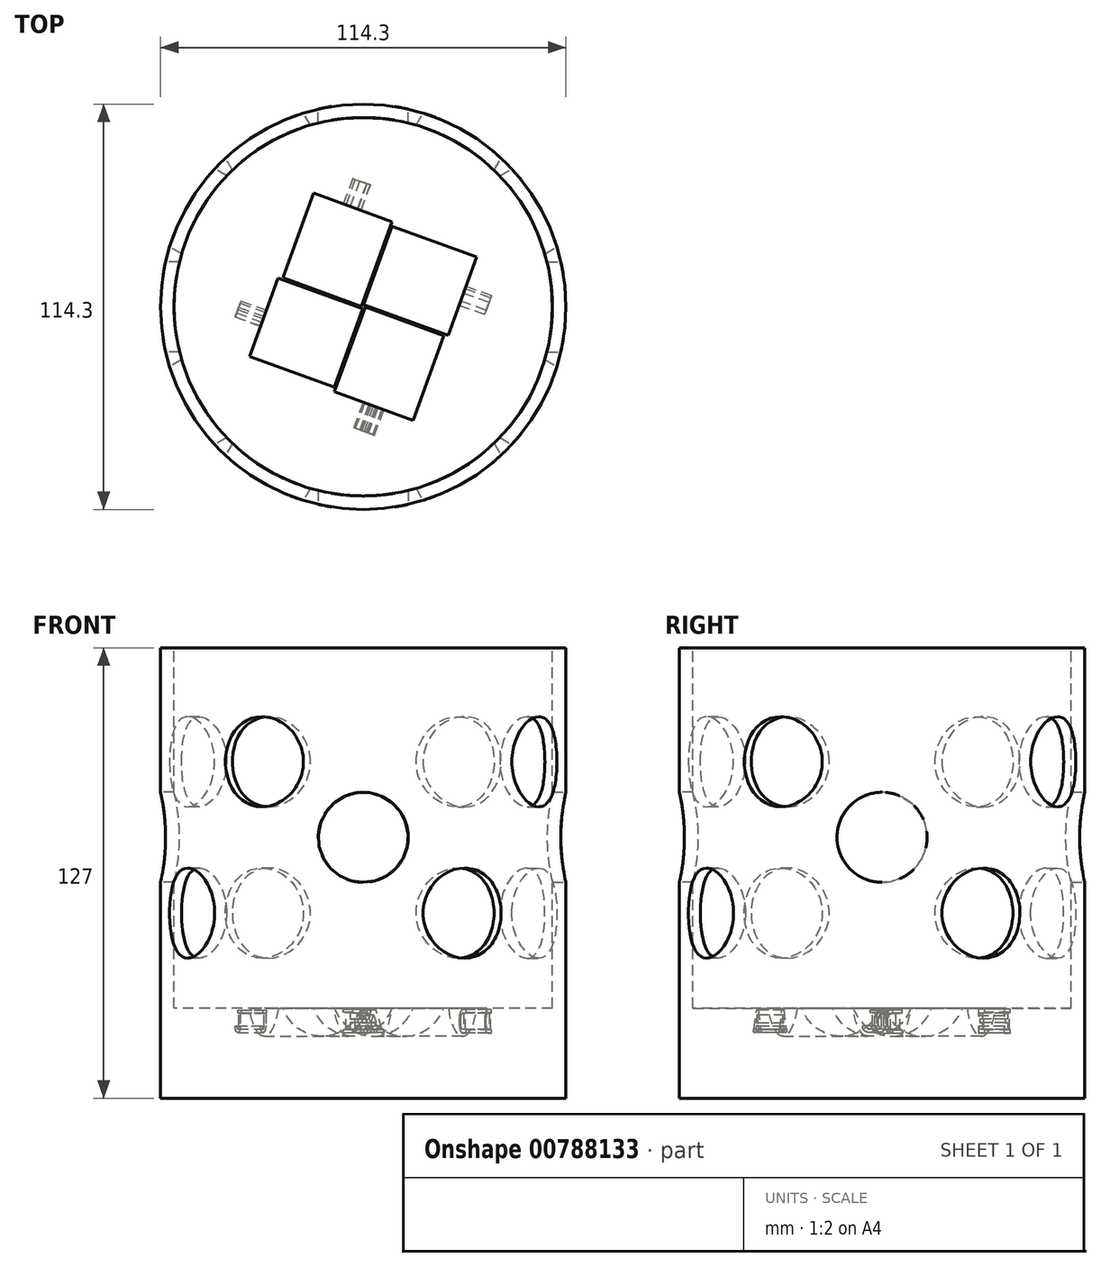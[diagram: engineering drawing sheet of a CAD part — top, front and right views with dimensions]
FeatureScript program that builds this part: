
annotation { "Feature Type Name" : "Feature", "Feature Type Description" : "" }
export const myFeature = defineFeature(function(context is Context, id is Id, definition is map)
    precondition{}
    {
        {
            var Q0;
            Q0=qCreatedBy(makeId("Top.planeOp"),FACE);
            var sketch = newSketch(context, id + "F0", { "sketchPlane" : qUnion([Q0])});
            skCircle(sketch, "E0", {"center": v(0, 0) * mm, "radius": 57.15 * mm});
            skSolve(sketch);
        }
        {
            var Q0;
            Q0=makeQuery(id+"F0.imprint","IMPRINT",FACE,{"disambiguationData":[TD([[makeQuery(id+"F0.imprint","IMPRINT",EDGE,{"derivedFrom":sQuery(id+"F0.wireOp",EDGE,"E0")}),1.0]])]});
            var Q1;
            Q1=sQuery(id+"F0.wireOp",EDGE,"E0");
            extrude(context, id + "F1", {"entities" : qUnion([Q0]), "surfaceEntities" : qUnion([Q1]), "depth" : 127 * mm, "offsetDistance" : 25.4 * mm});
        }
        {
            var Q0;
            Q0=makeQuery(id+"F1.opExtrude","CAP_FACE",FACE,{"disambiguationData":[OSD([sQuery(id+"F0.wireOp",EDGE,"E0")])],"isStart":false});
            var sketch = newSketch(context, id + "F2", { "sketchPlane" : qUnion([Q0])});
            skCircle(sketch, "E1", {"center": v(0, 0) * mm, "radius": 53.34 * mm});
            skSolve(sketch);
        }
        {
            var Q0;
            Q0=makeQuery(id+"F2.imprint","IMPRINT",FACE,{"disambiguationData":[TD([[makeQuery(id+"F2.imprint","IMPRINT",EDGE,{"derivedFrom":sQuery(id+"F2.wireOp",EDGE,"E1")}),1.0]])]});
            extrude(context, id + "F3", {"entities" : qUnion([Q0]), "operationType" : NewBodyOperationType.REMOVE, "oppositeDirection" : true, "depth" : 101.6 * mm, "offsetDistance" : 25.4 * mm});
        }
        {
            var Q0;
            Q0=qCreatedBy(makeId("Front.planeOp"),FACE);
            cPlane(context, id + "F4", {"entities" : qUnion([Q0]), "cplaneType" : CPlaneType.OFFSET, "offset" : 57.15 * mm, "width" : 152.4 * mm, "height" : 152.4 * mm});
        }
        {
            var Q0;
            Q0=qCreatedBy(id+"F4.planeOp",FACE);
            var sketch = newSketch(context, id + "F5", { "sketchPlane" : qUnion([Q0])});
            skCircle(sketch, "E2", {"center": v(0, 73.56) * mm, "radius": 12.7 * mm});
            skSolve(sketch);
        }
        {
            var Q0;
            Q0=makeQuery(id+"F5.imprint","IMPRINT",FACE,{"disambiguationData":[TD([[makeQuery(id+"F5.imprint","IMPRINT",EDGE,{"derivedFrom":sQuery(id+"F5.wireOp",EDGE,"E2")}),1.0]])]});
            extrude(context, id + "F6", {"entities" : qUnion([Q0]), "oppositeDirection" : true, "depth" : 25.4 * mm, "offsetDistance" : 25.4 * mm});
        }
        {
            var Q0;
            Q0=qCreatedBy(makeId("Front.planeOp"),FACE);
            var sketch = newSketch(context, id + "F7", { "sketchPlane" : qUnion([Q0])});
            skLineSegment(sketch, "E3", {"start": v(0, 0) * mm, "end": v(0, 71.78) * mm});
            skSolve(sketch);
        }
        {
            var Q0;
            Q0=makeQuery(id+"F6.opExtrude","SWEPT_BODY",BODY,{"disambiguationData":[OSD([sQuery(id+"F5.wireOp",EDGE,"E2")])]});
            var Q1;
            Q1=sQuery(id+"F7.wireOp",EDGE,"E3");
            circularPattern(context, id + "F8", {"entities" : qUnion([Q0]), "axis" : qUnion([Q1]), "angle" : 360 * degree, "instanceCount" : 4, "equalSpace" : true});
        }
        {
            var Q0;
            Q0=makeQuery(id+"F6.opExtrude","SWEPT_BODY",BODY,{"disambiguationData":[OSD([sQuery(id+"F5.wireOp",EDGE,"E2")])]});
            var Q1;
            Q1=makeQuery(id+"F8.opPattern","COPY",BODY,{"derivedFrom":makeQuery(id+"F6.opExtrude","SWEPT_BODY",BODY,{"disambiguationData":[OSD([sQuery(id+"F5.wireOp",EDGE,"E2")])]}),"instanceName":"3"});
            var Q2;
            Q2=makeQuery(id+"F8.opPattern","COPY",BODY,{"derivedFrom":makeQuery(id+"F6.opExtrude","SWEPT_BODY",BODY,{"disambiguationData":[OSD([sQuery(id+"F5.wireOp",EDGE,"E2")])]}),"instanceName":"2"});
            var Q3;
            Q3=makeQuery(id+"F8.opPattern","COPY",BODY,{"derivedFrom":makeQuery(id+"F6.opExtrude","SWEPT_BODY",BODY,{"disambiguationData":[OSD([sQuery(id+"F5.wireOp",EDGE,"E2")])]}),"instanceName":"1"});
            var Q4;
            Q4=makeQuery(id+"F1.opExtrude","SWEPT_BODY",BODY,{"disambiguationData":[OSD([sQuery(id+"F0.wireOp",EDGE,"E0")])]});
            booleanBodies(context, id + "F9", {"operationType" : BooleanOperationType.SUBTRACTION, "tools" : qUnion([Q0, Q1, Q2, Q3]), "targets" : qUnion([Q4])});
        }
        {
            var Q0;
            Q0=makeQuery(id+"F1.opExtrude","CAP_EDGE",EDGE,{"disambiguationData":[OSD([sQuery(id+"F0.wireOp",EDGE,"E0")])],"isStart":false});
            cPlane(context, id + "F10", {"entities" : qUnion([Q0]), "cplaneType" : CPlaneType.LINE_ANGLE, "offset" : 25.4 * mm, "angle" : 60 * degree, "width" : 152.4 * mm, "height" : 152.4 * mm});
        }
        {
            var Q0;
            Q0=qCreatedBy(id+"F10.planeOp",FACE);
            cPlane(context, id + "F11", {"entities" : qUnion([Q0]), "cplaneType" : CPlaneType.OFFSET, "offset" : 57.15 * mm, "width" : 152.4 * mm, "height" : 152.4 * mm});
        }
        {
            var Q0;
            Q0=qCreatedBy(id+"F11.planeOp",FACE);
            var sketch = newSketch(context, id + "F12", { "sketchPlane" : qUnion([Q0])});
            skCircle(sketch, "E4", {"center": v(0, 94.86) * mm, "radius": 12.7 * mm});
            skSolve(sketch);
        }
        {
            var Q0;
            Q0=makeQuery(id+"F12.imprint","IMPRINT",FACE,{"disambiguationData":[TD([[makeQuery(id+"F12.imprint","IMPRINT",EDGE,{"derivedFrom":sQuery(id+"F12.wireOp",EDGE,"E4")}),1.0]])]});
            extrude(context, id + "F13", {"entities" : qUnion([Q0]), "oppositeDirection" : true, "depth" : 25.4 * mm, "offsetDistance" : 25.4 * mm});
        }
        {
            var Q0;
            Q0=makeQuery(id+"F13.opExtrude","SWEPT_BODY",BODY,{"disambiguationData":[OSD([sQuery(id+"F12.wireOp",EDGE,"E4")])]});
            var Q1;
            Q1=makeQuery(id+"F1.opExtrude","SWEPT_FACE",FACE,{"disambiguationData":[OSD([sQuery(id+"F0.wireOp",EDGE,"E0")])]});
            circularPattern(context, id + "F14", {"entities" : qUnion([Q0]), "axis" : qUnion([Q1]), "angle" : 360 * degree, "instanceCount" : 4, "equalSpace" : true, "isCentered" : true});
        }
        {
            var Q0;
            Q0=makeQuery(id+"F14.opPattern","COPY",BODY,{"derivedFrom":makeQuery(id+"F13.opExtrude","SWEPT_BODY",BODY,{"disambiguationData":[OSD([sQuery(id+"F12.wireOp",EDGE,"E4")])]}),"instanceName":"-1"});
            var Q1;
            Q1=makeQuery(id+"F13.opExtrude","SWEPT_BODY",BODY,{"disambiguationData":[OSD([sQuery(id+"F12.wireOp",EDGE,"E4")])]});
            var Q2;
            Q2=makeQuery(id+"F14.opPattern","COPY",BODY,{"derivedFrom":makeQuery(id+"F13.opExtrude","SWEPT_BODY",BODY,{"disambiguationData":[OSD([sQuery(id+"F12.wireOp",EDGE,"E4")])]}),"instanceName":"-3"});
            var Q3;
            Q3=makeQuery(id+"F14.opPattern","COPY",BODY,{"derivedFrom":makeQuery(id+"F13.opExtrude","SWEPT_BODY",BODY,{"disambiguationData":[OSD([sQuery(id+"F12.wireOp",EDGE,"E4")])]}),"instanceName":"-2"});
            var Q4;
            Q4=makeQuery(id+"F1.opExtrude","SWEPT_BODY",BODY,{"disambiguationData":[OSD([sQuery(id+"F0.wireOp",EDGE,"E0")])]});
            booleanBodies(context, id + "F15", {"operationType" : BooleanOperationType.SUBTRACTION, "tools" : qUnion([Q0, Q1, Q2, Q3]), "targets" : qUnion([Q4])});
        }
        {
            var Q0;
            Q0=makeQuery(id+"F14.opPattern","COPY",BODY,{"derivedFrom":makeQuery(id+"F13.opExtrude","SWEPT_BODY",BODY,{"disambiguationData":[OSD([sQuery(id+"F12.wireOp",EDGE,"E4")])]}),"instanceName":"3"});
            var Q1;
            Q1=makeQuery(id+"F14.opPattern","COPY",BODY,{"derivedFrom":makeQuery(id+"F13.opExtrude","SWEPT_BODY",BODY,{"disambiguationData":[OSD([sQuery(id+"F12.wireOp",EDGE,"E4")])]}),"instanceName":"1"});
            var Q2;
            Q2=makeQuery(id+"F14.opPattern","COPY",BODY,{"derivedFrom":makeQuery(id+"F13.opExtrude","SWEPT_BODY",BODY,{"disambiguationData":[OSD([sQuery(id+"F12.wireOp",EDGE,"E4")])]}),"instanceName":"2"});
            var Q3;
            Q3=makeQuery(id+"F1.opExtrude","SWEPT_BODY",BODY,{"disambiguationData":[OSD([sQuery(id+"F0.wireOp",EDGE,"E0")])]});
            booleanBodies(context, id + "F16", {"operationType" : BooleanOperationType.SUBTRACTION, "tools" : qUnion([Q0, Q1, Q2]), "targets" : qUnion([Q3])});
        }
        {
            var Q0;
            Q0=makeQuery(id+"F1.opExtrude","SWEPT_FACE",FACE,{"disambiguationData":[OSD([sQuery(id+"F0.wireOp",EDGE,"E0")])]});
            cPlane(context, id + "F17", {"entities" : qUnion([Q0]), "cplaneType" : CPlaneType.LINE_ANGLE, "offset" : 25.4 * mm, "angle" : 150 * degree, "width" : 152.4 * mm, "height" : 152.4 * mm});
        }
        {
            var Q0;
            Q0=qCreatedBy(id+"F17.planeOp",FACE);
            cPlane(context, id + "F18", {"entities" : qUnion([Q0]), "cplaneType" : CPlaneType.OFFSET, "offset" : 57.15 * mm, "oppositeDirection" : true, "width" : 152.4 * mm, "height" : 152.4 * mm});
        }
        {
            var Q0;
            Q0=qCreatedBy(id+"F18.planeOp",FACE);
            var sketch = newSketch(context, id + "F19", { "sketchPlane" : qUnion([Q0])});
            skCircle(sketch, "E5", {"center": v(0, 52.2) * mm, "radius": 12.7 * mm});
            skSolve(sketch);
        }
        {
            var Q0;
            Q0=makeQuery(id+"F19.imprint","IMPRINT",FACE,{"disambiguationData":[TD([[makeQuery(id+"F19.imprint","IMPRINT",EDGE,{"derivedFrom":sQuery(id+"F19.wireOp",EDGE,"E5")}),1.0]])]});
            extrude(context, id + "F20", {"entities" : qUnion([Q0]), "depth" : 25.4 * mm, "offsetDistance" : 25.4 * mm});
        }
        {
            var Q0;
            Q0=makeQuery(id+"F20.opExtrude","SWEPT_BODY",BODY,{"disambiguationData":[OSD([sQuery(id+"F19.wireOp",EDGE,"E5")])]});
            var Q1;
            Q1=makeQuery(id+"F1.opExtrude","SWEPT_FACE",FACE,{"disambiguationData":[OSD([sQuery(id+"F0.wireOp",EDGE,"E0")])]});
            circularPattern(context, id + "F21", {"entities" : qUnion([Q0]), "axis" : qUnion([Q1]), "angle" : 360 * degree, "instanceCount" : 4, "equalSpace" : true});
        }
        {
            var Q0;
            Q0=makeQuery(id+"F20.opExtrude","SWEPT_BODY",BODY,{"disambiguationData":[OSD([sQuery(id+"F19.wireOp",EDGE,"E5")])]});
            var Q1;
            Q1=makeQuery(id+"F21.opPattern","COPY",BODY,{"derivedFrom":makeQuery(id+"F20.opExtrude","SWEPT_BODY",BODY,{"disambiguationData":[OSD([sQuery(id+"F19.wireOp",EDGE,"E5")])]}),"instanceName":"3"});
            var Q2;
            Q2=makeQuery(id+"F21.opPattern","COPY",BODY,{"derivedFrom":makeQuery(id+"F20.opExtrude","SWEPT_BODY",BODY,{"disambiguationData":[OSD([sQuery(id+"F19.wireOp",EDGE,"E5")])]}),"instanceName":"2"});
            var Q3;
            Q3=makeQuery(id+"F21.opPattern","COPY",BODY,{"derivedFrom":makeQuery(id+"F20.opExtrude","SWEPT_BODY",BODY,{"disambiguationData":[OSD([sQuery(id+"F19.wireOp",EDGE,"E5")])]}),"instanceName":"1"});
            var Q4;
            Q4=makeQuery(id+"F1.opExtrude","SWEPT_BODY",BODY,{"disambiguationData":[OSD([sQuery(id+"F0.wireOp",EDGE,"E0")])]});
            booleanBodies(context, id + "F22", {"operationType" : BooleanOperationType.SUBTRACTION, "tools" : qUnion([Q0, Q1, Q2, Q3]), "targets" : qUnion([Q4])});
        }
        {
            var Q0;
            Q0=makeQuery(id+"F1.opExtrude","SWEPT_FACE",FACE,{"disambiguationData":[OSD([sQuery(id+"F0.wireOp",EDGE,"E0")])]});
            cPlane(context, id + "F23", {"entities" : qUnion([Q0]), "cplaneType" : CPlaneType.LINE_ANGLE, "offset" : 25.4 * mm, "angle" : 20 * degree, "width" : 152.4 * mm, "height" : 152.4 * mm});
        }
        {
            var Q0;
            Q0=qCreatedBy(id+"F23.planeOp",FACE);
            cPlane(context, id + "F24", {"entities" : qUnion([Q0]), "cplaneType" : CPlaneType.OFFSET, "offset" : 4.5 / 50.8 * mm, "oppositeDirection" : true, "width" : 152.4 * mm, "height" : 152.4 * mm});
        }
        {
            var Q0;
            Q0=qCreatedBy(id+"F24.planeOp",FACE);
            var sketch = newSketch(context, id + "F25", { "sketchPlane" : qUnion([Q0])});
            skCircle(sketch, "E6", {"center": v(12.34, 30.17) * mm, "radius": 12.7 * mm});
            skSolve(sketch);
        }
        {
            var Q0;
            Q0=makeQuery(id+"F25.imprint","IMPRINT",FACE,{"disambiguationData":[TD([[makeQuery(id+"F25.imprint","IMPRINT",EDGE,{"derivedFrom":sQuery(id+"F25.wireOp",EDGE,"E6")}),1.0]])]});
            extrude(context, id + "F26", {"entities" : qUnion([Q0]), "depth" : 25.4 * mm, "offsetDistance" : 25.4 * mm});
        }
        {
            var Q0;
            Q0=makeQuery(id+"F26.opExtrude","SWEPT_BODY",BODY,{"disambiguationData":[OSD([sQuery(id+"F25.wireOp",EDGE,"E6")])]});
            var Q1;
            Q1=makeQuery(id+"F1.opExtrude","SWEPT_FACE",FACE,{"disambiguationData":[OSD([sQuery(id+"F0.wireOp",EDGE,"E0")])]});
            circularPattern(context, id + "F27", {"entities" : qUnion([Q0]), "axis" : qUnion([Q1]), "angle" : 360 * degree, "instanceCount" : 4, "equalSpace" : true});
        }
        {
            var Q0;
            Q0=makeQuery(id+"F26.opExtrude","SWEPT_BODY",BODY,{"disambiguationData":[OSD([sQuery(id+"F25.wireOp",EDGE,"E6")])]});
            var Q1;
            Q1=makeQuery(id+"F27.opPattern","COPY",BODY,{"derivedFrom":makeQuery(id+"F26.opExtrude","SWEPT_BODY",BODY,{"disambiguationData":[OSD([sQuery(id+"F25.wireOp",EDGE,"E6")])]}),"instanceName":"2"});
            var Q2;
            Q2=makeQuery(id+"F27.opPattern","COPY",BODY,{"derivedFrom":makeQuery(id+"F26.opExtrude","SWEPT_BODY",BODY,{"disambiguationData":[OSD([sQuery(id+"F25.wireOp",EDGE,"E6")])]}),"instanceName":"1"});
            var Q3;
            Q3=makeQuery(id+"F27.opPattern","COPY",BODY,{"derivedFrom":makeQuery(id+"F26.opExtrude","SWEPT_BODY",BODY,{"disambiguationData":[OSD([sQuery(id+"F25.wireOp",EDGE,"E6")])]}),"instanceName":"3"});
            var Q4;
            Q4=makeQuery(id+"F1.opExtrude","SWEPT_BODY",BODY,{"disambiguationData":[OSD([sQuery(id+"F0.wireOp",EDGE,"E0")])]});
            booleanBodies(context, id + "F28", {"operationType" : BooleanOperationType.SUBTRACTION, "tools" : qUnion([Q0, Q1, Q2, Q3]), "targets" : qUnion([Q4])});
        }
        {
            var Q0;
            Q0=makeQuery(id+"F28.opBoolean","COPY",FACE,{"derivedFrom":makeQuery(id+"F27.opPattern","COPY",FACE,{"derivedFrom":makeQuery(id+"F26.opExtrude","CAP_FACE",FACE,{"disambiguationData":[OSD([sQuery(id+"F25.wireOp",EDGE,"E6")])],"isStart":false}),"instanceName":"3"})});
            var sketch = newSketch(context, id + "F29", { "sketchPlane" : qUnion([Q0])});
            skText(sketch, "E7", { "text": "A", "fontName": "RobotoSlab-Bold.ttf"});
            const initialGuessF29  = {"E7": [-0.01554, 0.01864, 1, 0, 0.00647]};
            skSetInitialGuess(sketch, initialGuessF29);
            skSolve(sketch);
        }
        {
            var Q0;
            Q0=makeQuery(id+"F29.imprint","IMPRINT",FACE,{"disambiguationData":[TD([[makeQuery(id+"F29.imprint","IMPRINT",EDGE,{"derivedFrom":sQuery(id+"F29.wireOp",EDGE,"E7.sketch_text.stroke-0")}),-1.0]])]});
            extrude(context, id + "F30", {"entities" : qUnion([Q0]), "operationType" : NewBodyOperationType.REMOVE, "oppositeDirection" : true, "depth" : 7.62 * mm, "offsetDistance" : 25.4 * mm});
        }
        {
            var Q0;
            Q0=makeQuery(id+"F28.opBoolean","COPY",FACE,{"derivedFrom":makeQuery(id+"F26.opExtrude","CAP_FACE",FACE,{"disambiguationData":[OSD([sQuery(id+"F25.wireOp",EDGE,"E6")])],"isStart":false})});
            var sketch = newSketch(context, id + "F31", { "sketchPlane" : qUnion([Q0])});
            skText(sketch, "E8", { "text": "J", "fontName": "RobotoSlab-Bold.ttf"});
            const initialGuessF31  = {"E8": [-0.01523, 0.01862, 1, 0, 0.00633]};
            skSetInitialGuess(sketch, initialGuessF31);
            skSolve(sketch);
        }
        {
            var Q0;
            Q0=makeQuery(id+"F31.imprint","IMPRINT",FACE,{"disambiguationData":[TD([[makeQuery(id+"F31.imprint","IMPRINT",EDGE,{"derivedFrom":sQuery(id+"F31.wireOp",EDGE,"E8.sketch_text.stroke-0")}),-1.0]])]});
            extrude(context, id + "F32", {"entities" : qUnion([Q0]), "operationType" : NewBodyOperationType.REMOVE, "oppositeDirection" : true, "depth" : 7.62 * mm, "offsetDistance" : 25.4 * mm});
        }
        {
            var Q0;
            Q0=makeQuery(id+"F28.opBoolean","COPY",FACE,{"derivedFrom":makeQuery(id+"F27.opPattern","COPY",FACE,{"derivedFrom":makeQuery(id+"F26.opExtrude","CAP_FACE",FACE,{"disambiguationData":[OSD([sQuery(id+"F25.wireOp",EDGE,"E6")])],"isStart":false}),"instanceName":"2"})});
            var sketch = newSketch(context, id + "F33", { "sketchPlane" : qUnion([Q0])});
            skText(sketch, "E9", { "text": "D", "fontName": "RobotoSlab-Bold.ttf"});
            const initialGuessF33  = {"E9": [-0.0155, 0.01842, 1, 0, 0.00658]};
            skSetInitialGuess(sketch, initialGuessF33);
            skSolve(sketch);
        }
        {
            var Q0;
            Q0=makeQuery(id+"F33.imprint","IMPRINT",FACE,{"disambiguationData":[TD([[makeQuery(id+"F33.imprint","IMPRINT",EDGE,{"derivedFrom":sQuery(id+"F33.wireOp",EDGE,"E9.sketch_text.stroke-0")}),-1.0]])]});
            extrude(context, id + "F34", {"entities" : qUnion([Q0]), "operationType" : NewBodyOperationType.REMOVE, "oppositeDirection" : true, "depth" : 7.62 * mm, "offsetDistance" : 25.4 * mm});
        }
        {
            var Q0;
            Q0=makeQuery(id+"F28.opBoolean","COPY",FACE,{"derivedFrom":makeQuery(id+"F27.opPattern","COPY",FACE,{"derivedFrom":makeQuery(id+"F26.opExtrude","CAP_FACE",FACE,{"disambiguationData":[OSD([sQuery(id+"F25.wireOp",EDGE,"E6")])],"isStart":false}),"instanceName":"1"})});
            var sketch = newSketch(context, id + "F35", { "sketchPlane" : qUnion([Q0])});
            skText(sketch, "E10", { "text": "E", "fontName": "RobotoSlab-Bold.ttf"});
            const initialGuessF35  = {"E10": [-0.01541, 0.01842, 1, 0, 0.0067]};
            skSetInitialGuess(sketch, initialGuessF35);
            skSolve(sketch);
        }
        {
            var Q0;
            Q0=makeQuery(id+"F35.imprint","IMPRINT",FACE,{"disambiguationData":[TD([[makeQuery(id+"F35.imprint","IMPRINT",EDGE,{"derivedFrom":sQuery(id+"F35.wireOp",EDGE,"E10.sketch_text.stroke-0")}),-1.0]])]});
            extrude(context, id + "F36", {"entities" : qUnion([Q0]), "operationType" : NewBodyOperationType.REMOVE, "oppositeDirection" : true, "depth" : 7.62 * mm, "offsetDistance" : 25.4 * mm});
        }
    });
